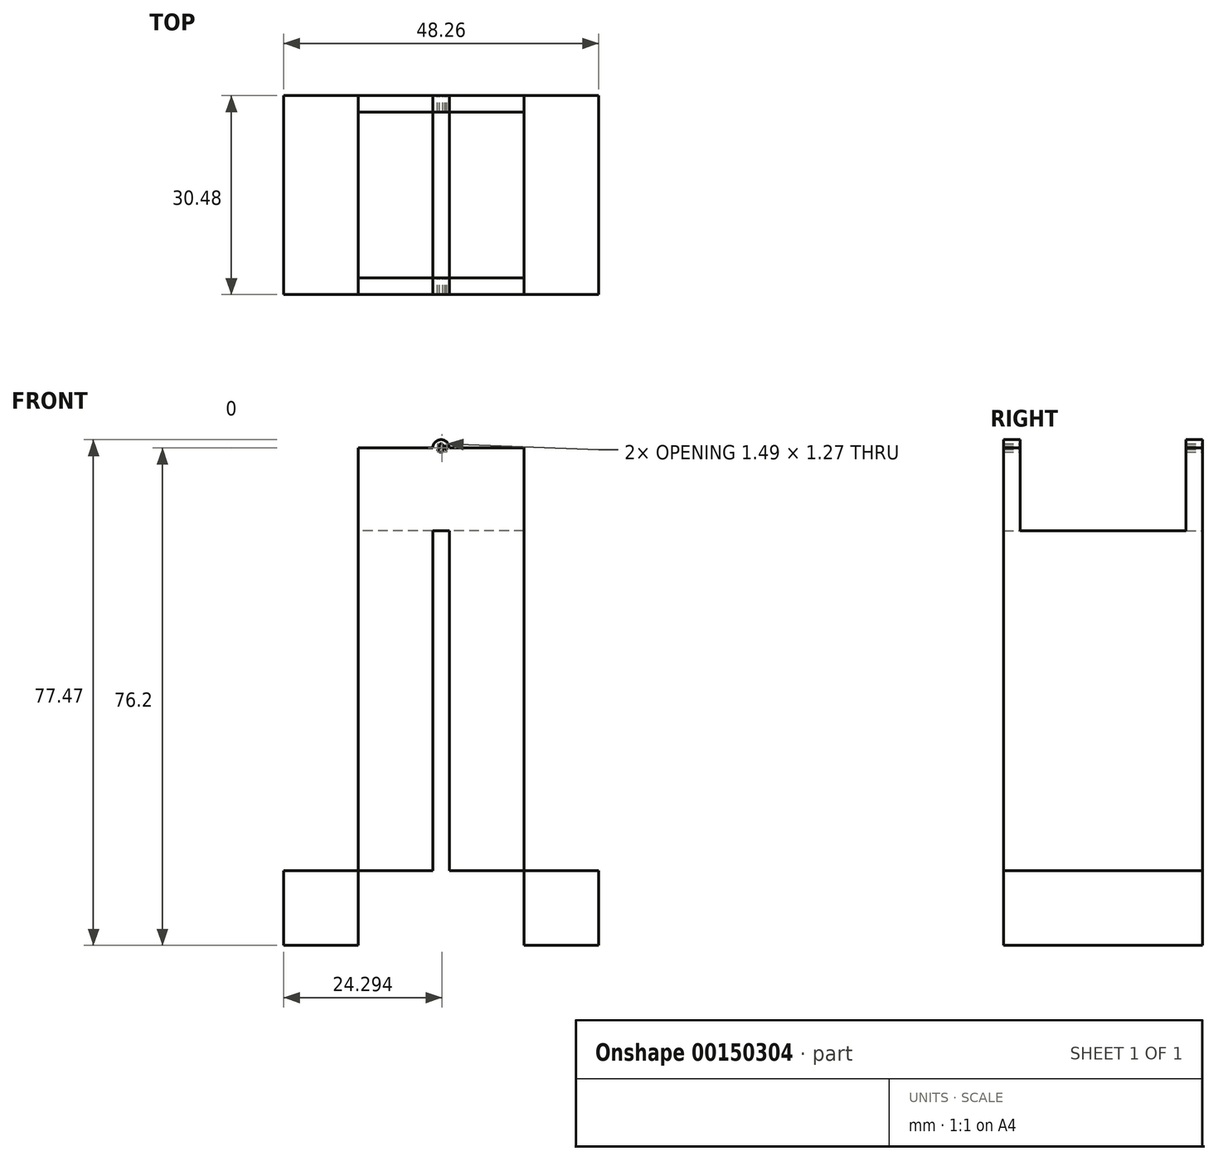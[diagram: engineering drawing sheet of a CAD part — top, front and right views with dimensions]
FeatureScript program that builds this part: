
annotation { "Feature Type Name" : "Feature", "Feature Type Description" : "" }
export const myFeature = defineFeature(function(context is Context, id is Id, definition is map)
    precondition{}
    {
        {
            var Q0;
            Q0=qCreatedBy(makeId("Front.planeOp"),FACE);
            var sketch = newSketch(context, id + "F0", { "sketchPlane" : qUnion([Q0])});
            skLineSegment(sketch, "E0.bottom", {"start": v(-12.7, 38.1) * mm, "end": v(12.7, 38.1) * mm});
            skLineSegment(sketch, "E0.top", {"start": v(-12.7, -38.1) * mm, "end": v(12.7, -38.1) * mm});
            skLineSegment(sketch, "E0.left", {"start": v(-12.7, 38.1) * mm, "end": v(-12.7, -38.1) * mm});
            skLineSegment(sketch, "E0.right", {"start": v(12.7, 38.1) * mm, "end": v(12.7, -38.1) * mm});
            skPoint(sketch, "E0.middle", {"position": v(0, 0) * mm});
            skLineSegment(sketch, "E1.bottom", {"start": v(1.27, -38.1) * mm, "end": v(-1.27, -38.1) * mm});
            skLineSegment(sketch, "E1.top", {"start": v(1.27, 25.4) * mm, "end": v(-1.27, 25.4) * mm});
            skLineSegment(sketch, "E1.left", {"start": v(1.27, -38.1) * mm, "end": v(1.27, 25.4) * mm});
            skLineSegment(sketch, "E1.right", {"start": v(-1.27, -38.1) * mm, "end": v(-1.27, 25.4) * mm});
            skLineSegment(sketch, "E2.bottom", {"start": v(-1.27, -38.1) * mm, "end": v(-24.13, -38.1) * mm});
            skLineSegment(sketch, "E2.top", {"start": v(-1.27, -26.67) * mm, "end": v(-24.13, -26.67) * mm});
            skLineSegment(sketch, "E2.left", {"start": v(-1.27, -38.1) * mm, "end": v(-1.27, -26.67) * mm});
            skLineSegment(sketch, "E2.right", {"start": v(-24.13, -38.1) * mm, "end": v(-24.13, -26.67) * mm});
            skLineSegment(sketch, "E3.bottom", {"start": v(1.27, -38.1) * mm, "end": v(24.13, -38.1) * mm});
            skLineSegment(sketch, "E3.top", {"start": v(1.27, -26.67) * mm, "end": v(24.13, -26.67) * mm});
            skLineSegment(sketch, "E3.left", {"start": v(1.27, -38.1) * mm, "end": v(1.27, -26.67) * mm});
            skLineSegment(sketch, "E3.right", {"start": v(24.13, -38.1) * mm, "end": v(24.13, -26.67) * mm});
            skCircle(sketch, "E4", {"center": v(0, 38.1) * mm, "radius": 1.27 * mm});
            skCircle(sketch, "E5", {"center": v(0, 38.1) * mm, "radius": 0.64 * mm});
            skLineSegment(sketch, "E6.bottom", {"start": v(0.9, 38.35) * mm, "end": v(-0.9, 38.35) * mm});
            skLineSegment(sketch, "E6.top", {"start": v(0.9, 37.85) * mm, "end": v(-0.9, 37.85) * mm});
            skLineSegment(sketch, "E6.left", {"start": v(0.9, 38.35) * mm, "end": v(0.9, 37.85) * mm});
            skLineSegment(sketch, "E6.right", {"start": v(-0.9, 38.35) * mm, "end": v(-0.9, 37.85) * mm});
            skLineSegment(sketch, "E7.bottom", {"start": v(-0.25, 38.82) * mm, "end": v(0.25, 38.82) * mm});
            skLineSegment(sketch, "E7.top", {"start": v(-0.25, 37.38) * mm, "end": v(0.25, 37.38) * mm});
            skLineSegment(sketch, "E7.left", {"start": v(-0.25, 38.82) * mm, "end": v(-0.25, 37.38) * mm});
            skLineSegment(sketch, "E7.right", {"start": v(0.25, 38.82) * mm, "end": v(0.25, 37.38) * mm});
            skSolve(sketch);
        }
        {
            var Q0;
            Q0=makeQuery(id+"F0.imprint","IMPRINT",FACE,{"disambiguationData":[TD([[makeQuery(id+"F0.imprint","IMPRINT",EDGE,{"derivedFrom":sQuery(id+"F0.wireOp",EDGE,"E0.bottom")}),-1.0]])]});
            var Q1;
            {var subQ5=sQuery(id+"F0.wireOp",EDGE,"E2.left");Q1=makeQuery(id+"F0.imprint","IMPRINT",FACE,{"disambiguationData":[TD([[makeQuery(id+"F0.imprint","IMPRINT",EDGE,{"derivedFrom":subQ5}),1.0]])]});}
            var Q2;
            {var subQ5=sQuery(id+"F0.wireOp",EDGE,"E2.right");Q2=makeQuery(id+"F0.imprint","IMPRINT",FACE,{"disambiguationData":[TD([[makeQuery(id+"F0.imprint","IMPRINT",EDGE,{"derivedFrom":subQ5}),-1.0]])]});}
            var Q3;
            {var subQ5=sQuery(id+"F0.wireOp",EDGE,"E3.left");Q3=makeQuery(id+"F0.imprint","IMPRINT",FACE,{"disambiguationData":[TD([[makeQuery(id+"F0.imprint","IMPRINT",EDGE,{"derivedFrom":subQ5}),-1.0]])]});}
            var Q4;
            {var subQ5=sQuery(id+"F0.wireOp",EDGE,"E3.right");Q4=makeQuery(id+"F0.imprint","IMPRINT",FACE,{"disambiguationData":[TD([[makeQuery(id+"F0.imprint","IMPRINT",EDGE,{"derivedFrom":subQ5}),1.0]])]});}
            var Q5;
            {var subQ5=sQuery(id+"F0.wireOp",EDGE,"E7.top");Q5=makeQuery(id+"F0.imprint","IMPRINT",FACE,{"disambiguationData":[TD([[makeQuery(id+"F0.imprint","IMPRINT",EDGE,{"derivedFrom":subQ5}),-1.0]])]});}
            var Q6;
            {var subQ5=sQuery(id+"F0.wireOp",EDGE,"E7.bottom");Q6=makeQuery(id+"F0.imprint","IMPRINT",FACE,{"disambiguationData":[TD([[makeQuery(id+"F0.imprint","IMPRINT",EDGE,{"derivedFrom":subQ5}),1.0]])]});}
            var Q7;
            {var subQ0=sQuery(id+"F0.wireOp",EDGE,"E6.right");var subQ1=sQuery(id+"F0.wireOp",EDGE,"E0.bottom");var subQ2=makeQuery(id+"F0.imprint","INTERSECT",VERTEX,{"derivedFrom":[subQ1,subQ0]});Q7=makeQuery(id+"F0.imprint","IMPRINT",FACE,{"disambiguationData":[TD([[makeQuery(id+"F0.imprint","IMPRINT",EDGE,{"disambiguationData":[TD([[subQ2,-1.0]])],"derivedFrom":subQ1}),-1.0]])]});}
            var Q8;
            {var subQ0=sQuery(id+"F0.wireOp",EDGE,"E6.right");var subQ1=sQuery(id+"F0.wireOp",EDGE,"E0.bottom");var subQ2=makeQuery(id+"F0.imprint","INTERSECT",VERTEX,{"derivedFrom":[subQ1,subQ0]});Q8=makeQuery(id+"F0.imprint","IMPRINT",FACE,{"disambiguationData":[TD([[makeQuery(id+"F0.imprint","IMPRINT",EDGE,{"disambiguationData":[TD([[subQ2,-1.0]])],"derivedFrom":subQ1}),1.0]])]});}
            var Q9;
            {var subQ0=sQuery(id+"F0.wireOp",EDGE,"E7.left");var subQ1=sQuery(id+"F0.wireOp",EDGE,"E5");var subQ2=makeQuery(id+"F0.imprint","INTERSECT",VERTEX,{"disambiguationData":[OD(0.0)],"derivedFrom":[subQ1,subQ0]});Q9=makeQuery(id+"F0.imprint","IMPRINT",FACE,{"disambiguationData":[TD([[makeQuery(id+"F0.imprint","IMPRINT",EDGE,{"disambiguationData":[TD([[subQ2,-1.0]])],"derivedFrom":subQ1}),1.0]])]});}
            var Q10;
            {var subQ0=sQuery(id+"F0.wireOp",EDGE,"E6.bottom");var subQ1=sQuery(id+"F0.wireOp",EDGE,"E5");var subQ2=makeQuery(id+"F0.imprint","INTERSECT",VERTEX,{"disambiguationData":[OD(0.0)],"derivedFrom":[subQ1,subQ0]});Q10=makeQuery(id+"F0.imprint","IMPRINT",FACE,{"disambiguationData":[TD([[makeQuery(id+"F0.imprint","IMPRINT",EDGE,{"disambiguationData":[TD([[subQ2,-1.0]])],"derivedFrom":subQ1}),1.0]])]});}
            var Q11;
            {var subQ0=sQuery(id+"F0.wireOp",EDGE,"E5");var subQ1=sQuery(id+"F0.wireOp",EDGE,"E0.bottom");var subQ2=makeQuery(id+"F0.imprint","INTERSECT",VERTEX,{"disambiguationData":[OD(1.0)],"derivedFrom":[subQ1,subQ0]});Q11=makeQuery(id+"F0.imprint","IMPRINT",FACE,{"disambiguationData":[TD([[makeQuery(id+"F0.imprint","IMPRINT",EDGE,{"disambiguationData":[TD([[subQ2,-1.0]])],"derivedFrom":subQ1}),1.0]])]});}
            var Q12;
            {var subQ0=sQuery(id+"F0.wireOp",EDGE,"E5");var subQ1=sQuery(id+"F0.wireOp",EDGE,"E0.bottom");var subQ2=makeQuery(id+"F0.imprint","INTERSECT",VERTEX,{"disambiguationData":[OD(1.0)],"derivedFrom":[subQ1,subQ0]});Q12=makeQuery(id+"F0.imprint","IMPRINT",FACE,{"disambiguationData":[TD([[makeQuery(id+"F0.imprint","IMPRINT",EDGE,{"disambiguationData":[TD([[subQ2,-1.0]])],"derivedFrom":subQ1}),-1.0]])]});}
            var Q13;
            {var subQ0=sQuery(id+"F0.wireOp",EDGE,"E7.right");var subQ1=sQuery(id+"F0.wireOp",EDGE,"E5");var subQ2=makeQuery(id+"F0.imprint","INTERSECT",VERTEX,{"disambiguationData":[OD(1.0)],"derivedFrom":[subQ1,subQ0]});Q13=makeQuery(id+"F0.imprint","IMPRINT",FACE,{"disambiguationData":[TD([[makeQuery(id+"F0.imprint","IMPRINT",EDGE,{"disambiguationData":[TD([[subQ2,-1.0]])],"derivedFrom":subQ1}),1.0]])]});}
            var Q14;
            {var subQ5=sQuery(id+"F0.wireOp",EDGE,"E7.top");Q14=makeQuery(id+"F0.imprint","IMPRINT",FACE,{"disambiguationData":[TD([[makeQuery(id+"F0.imprint","IMPRINT",EDGE,{"derivedFrom":subQ5}),1.0]])]});}
            var Q15;
            {var subQ5=sQuery(id+"F0.wireOp",EDGE,"E7.bottom");Q15=makeQuery(id+"F0.imprint","IMPRINT",FACE,{"disambiguationData":[TD([[makeQuery(id+"F0.imprint","IMPRINT",EDGE,{"derivedFrom":subQ5}),-1.0]])]});}
            var Q16;
            {var subQ0=sQuery(id+"F0.wireOp",EDGE,"E6.top");var subQ1=sQuery(id+"F0.wireOp",EDGE,"E5");var subQ2=makeQuery(id+"F0.imprint","INTERSECT",VERTEX,{"disambiguationData":[OD(0.0)],"derivedFrom":[subQ1,subQ0]});Q16=makeQuery(id+"F0.imprint","IMPRINT",FACE,{"disambiguationData":[TD([[makeQuery(id+"F0.imprint","IMPRINT",EDGE,{"disambiguationData":[TD([[subQ2,-1.0]])],"derivedFrom":subQ1}),1.0]])]});}
            extrude(context, id + "F1", {"entities" : qUnion([Q0, Q1, Q2, Q3, Q4, Q5, Q6, Q7, Q8, Q9, Q10, Q11, Q12, Q13, Q14, Q15, Q16]), "depth" : 30.48 * mm});
        }
        {
            var Q0;
            Q0=makeQuery(id+"F1.opExtrude","SWEPT_FACE",FACE,{"disambiguationData":[OSD([sQuery(id+"F0.wireOp",EDGE,"E0.bottom")])]});
            var sketch = newSketch(context, id + "F2", { "sketchPlane" : qUnion([Q0])});
            skLineSegment(sketch, "E8", {"start": v(-6.98, 0) * mm, "end": v(-6.98, -15.24) * mm});
            skPoint(sketch, "E8.endSnap0", {"position": v(-6.98, 0) * mm});
            skLineSegment(sketch, "E9.bottom", {"start": v(12.7, -2.54) * mm, "end": v(-26.67, -2.54) * mm});
            skLineSegment(sketch, "E9.top", {"start": v(12.7, -27.94) * mm, "end": v(-26.67, -27.94) * mm});
            skLineSegment(sketch, "E9.left", {"start": v(12.7, -2.54) * mm, "end": v(12.7, -27.94) * mm});
            skLineSegment(sketch, "E9.right", {"start": v(-26.67, -2.54) * mm, "end": v(-26.67, -27.94) * mm});
            skPoint(sketch, "E9.middle", {"position": v(-6.98, -15.24) * mm});
            skSolve(sketch);
        }
        {
            var Q0;
            Q0 = qSketchRegion(id + "F2", true);
            extrude(context, id + "F3", {"entities" : qUnion([Q0]), "operationType" : NewBodyOperationType.REMOVE, "oppositeDirection" : true, "depth" : 12.7 * mm, "hasSecondDirection" : true, "secondDirectionOppositeDirection" : false, "secondDirectionDepth" : 25.4 * mm});
        }
    });
